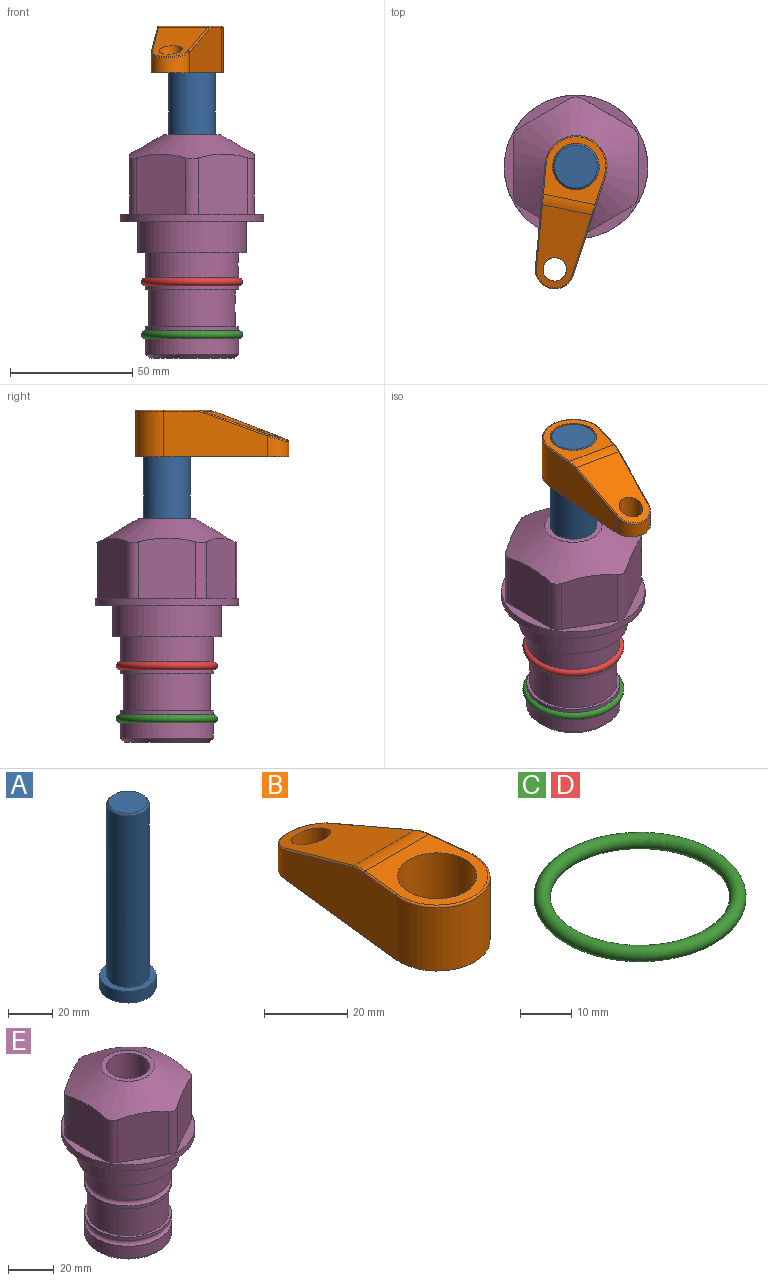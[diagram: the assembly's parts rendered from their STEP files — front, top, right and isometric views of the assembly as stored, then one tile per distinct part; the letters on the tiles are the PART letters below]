
ASSEMBLY  parts=5 mates=3
PART A: 6 faces, bbox 25.4x25.4x101.6 mm
  f0: plane 17.46x17.46mm, normal (0,0,1), area 239.5mm2, adj f5
  f1: plane 25.4x25.4mm, normal (0,0,-1), area 506.7mm2, adj f2
  f2: cylinder r=12.7mm len=25.4mm, axis (0,0,1), area 506.7mm2, adj f1,f3
  f3: plane 25.4x25.4mm, normal (0,0,1), area 221.7mm2, adj f2,f4
  f4: cylinder r=9.53mm len=94.46mm, axis (0,0,1), area 5653mm2, adj f3,f5
  f5: cone r=8.73mm half-angle=45deg, axis (0,0,-1), area 64.4mm2, adj f0,f4
PART B: 44 faces, bbox 27.5x64.5x19.1 mm
  f0: plane 2.3x0.95mm, normal (0,0,-1), area 1mm2, adj f25,f30,f34
  f1: plane 63.5x25.4mm, normal (0,0,-1), area 561.7mm2, adj f2,f3,f4,f5,f6,f7,f19,f20
  f2: cylinder r=12.7mm len=25.4mm, axis (0,0,-1), area 792.2mm2, adj f1,f3,f5,f13
  f3: plane 42.33x18.54mm, normal (0.99,0.11,0), area 647mm2, adj f1,f2,f4,f11,f12,f14
  f4: cylinder r=7.94mm len=15.78mm, axis (0,0,-1), area 158.6mm2, adj f1,f3,f5,f16
  f5: plane 42.33x18.54mm, normal (-0.99,0.11,0), area 647mm2, adj f1,f2,f4,f15,f17,f18
  f6: cylinder r=9.53mm len=19.05mm, axis (0,0,-1), area 1140.1mm2, adj f1,f8
  f7: cylinder r=4.76mm len=10.98mm, axis (0,0,-1), area 276.1mm2, adj f1,f9
  f8: plane 25.83x24.38mm, normal (0,0,1), area 262.2mm2, adj f6,f10,f11,f13,f15
  f9: plane 32.49x20.55mm, normal (0,0.34,0.94), area 489.9mm2, adj f7,f10,f14,f16,f18
  f10: cylinder r=12.7mm len=21.49mm, axis (-1,0,0), area 93.2mm2, adj f8,f9,f12,f17
  f11: cylinder r=0.51mm len=12.34mm, axis (0.11,-0.99,0), area 9.9mm2, adj f3,f8,f12,f13
  f12: bspline ~7.62x1.64mm, area 3.5mm2, adj f3,f10,f11,f14
  f13: torus R=12.19mm, axis (0,0,1), area 33.6mm2, adj f2,f8,f11,f15
  f14: cylinder r=0.51mm len=26.01mm, axis (0.1,-0.93,0.34), area 21.6mm2, adj f3,f9,f12,f16
  f15: cylinder r=0.51mm len=12.34mm, axis (0.11,0.99,0), area 9.9mm2, adj f5,f8,f13,f17
  f16: bspline ~15.78x7.05mm, area 15.7mm2, adj f4,f9,f14,f18
  f17: bspline ~7.62x1.64mm, area 3.5mm2, adj f5,f10,f15,f18
  f18: cylinder r=0.51mm len=26.01mm, axis (0.1,0.93,-0.34), area 21.6mm2, adj f5,f9,f16,f17
  f19: plane 21.6x14.29mm, normal (-0.99,-0.11,0), area 242.6mm2, adj f1,f26,f28,f34,f36,f38
  f20: plane 21.6x14.29mm, normal (0.99,-0.11,0), area 242.6mm2, adj f1,f27,f29,f37,f39,f41
  f21: cylinder r=12.7mm len=14.29mm, axis (0,0,-1), area 173.2mm2, adj f1,f26,f27,f30,f31,f33
  f22: cylinder r=7.94mm len=7.63mm, axis (0,0,-1), area 53.8mm2, adj f1,f28,f29,f42
  f23: plane 2.3x0.95mm, normal (0,0,-1), area 1mm2, adj f25,f33,f37
  f24: plane 17.94x12.32mm, normal (0,-0.34,-0.94), area 191.2mm2, adj f25,f38,f41,f42
  f25: cylinder r=9.53mm len=12.93mm, axis (-1,0,0), area 37.5mm2, adj f0,f23,f24,f31,f36,f39
  f26: cylinder r=1.59mm len=14.29mm, axis (0,0,-1), area 49mm2, adj f1,f19,f21,f32
  f27: cylinder r=1.59mm len=14.29mm, axis (0,0,-1), area 49mm2, adj f1,f20,f21,f35
  f28: cylinder r=1.59mm len=7.28mm, axis (0,0,-1), area 22.1mm2, adj f1,f19,f22,f40
  f29: cylinder r=1.59mm len=7.28mm, axis (0,0,-1), area 22.1mm2, adj f1,f20,f22,f43
  f30: torus R=14.29mm, axis (0,0,1), area 5.8mm2, adj f0,f21,f31,f32
  f31: bspline ~11.06x2.73mm, area 20.8mm2, adj f21,f25,f30,f33
  f32: sphere r=1.59mm, area 5.4mm2, adj f26,f30,f34
  f33: torus R=14.29mm, axis (0,0,1), area 5.8mm2, adj f21,f23,f31,f35
  f34: cylinder r=1.59mm len=1.68mm, axis (-0.11,0.99,0), area 2.4mm2, adj f0,f19,f32,f36
  f35: sphere r=1.59mm, area 5.4mm2, adj f27,f33,f37
  f36: bspline ~5.82x2.33mm, area 7.7mm2, adj f19,f25,f34,f38
  f37: cylinder r=1.59mm len=1.68mm, axis (0.11,0.99,0), area 2.4mm2, adj f20,f23,f35,f39
  f38: cylinder r=1.59mm len=18.33mm, axis (0.1,-0.93,0.34), area 46.7mm2, adj f19,f24,f36,f40
  f39: bspline ~5.82x2.33mm, area 7.7mm2, adj f20,f25,f37,f41
  f40: sphere r=1.59mm, area 3.6mm2, adj f28,f38,f42
  f41: cylinder r=1.59mm len=18.33mm, axis (0.1,0.93,-0.34), area 46.7mm2, adj f20,f24,f39,f43
  f42: bspline ~8.31x1.84mm, area 15.3mm2, adj f22,f24,f40,f43
  f43: sphere r=1.59mm, area 3.6mm2, adj f29,f41,f42
PART C: 1 faces, bbox 44.7x44.7x3.2 mm
  f0: torus R=19.05mm, axis (0,0,1), area 1193.9mm2
PART D: same geometry as C
PART E: 36 faces, bbox 58.7x58.7x91.2 mm
  f0: cylinder r=17.78mm len=35.56mm, axis (0,0,1), area 1670.8mm2, adj f23,f24,f31
  f1: cylinder r=19.05mm len=38.1mm, axis (0,0,1), area 1191.9mm2, adj f26,f27,f30
  f2: plane 58.66x58.66mm, normal (0,0,-1), area 1150.6mm2, adj f3,f28
  f3: cylinder r=29.33mm len=58.66mm, axis (0,0,-1), area 585.1mm2, adj f2,f4
  f4: plane 58.66x58.66mm, normal (0,0,1), area 475.9mm2, adj f3,f5,f6,f7,f8,f9,f10,f11
  f5: plane 24.5x20.32mm, normal (-0.5,0.87,0), area 562.8mm2, adj f4,f15,f16,f17
  f6: plane 24.5x20.32mm, normal (0.5,0.87,0), area 562.8mm2, adj f4,f14,f15,f17
  f7: plane 24.5x23.48mm, normal (1,0,0), area 562.8mm2, adj f4,f13,f14,f17
  f8: plane 24.5x20.32mm, normal (0.5,-0.87,0), area 562.8mm2, adj f4,f12,f13,f17
  f9: plane 24.5x20.32mm, normal (-0.5,-0.87,0), area 562.8mm2, adj f4,f11,f12,f17
  f10: plane 24.5x23.48mm, normal (-1,0,0), area 562.8mm2, adj f4,f11,f16,f17
  f11: cylinder r=5.08mm len=23.01mm, axis (0,0,-1), area 121.2mm2, adj f4,f9,f10,f17
  f12: cylinder r=5.08mm len=23.01mm, axis (0,0,-1), area 121.2mm2, adj f4,f8,f9,f17
  f13: cylinder r=5.08mm len=23.01mm, axis (0,0,-1), area 121.2mm2, adj f4,f7,f8,f17
  f14: cylinder r=5.08mm len=23.01mm, axis (0,0,-1), area 121.2mm2, adj f4,f6,f7,f17
  f15: cylinder r=5.08mm len=23.01mm, axis (0,0,-1), area 121.2mm2, adj f4,f5,f6,f17
  f16: cylinder r=5.08mm len=23.01mm, axis (0,0,-1), area 121.2mm2, adj f4,f5,f10,f17
  f17: cone r=11.73mm half-angle=60deg, axis (0,0,-1), area 2071.8mm2, adj f5,f6,f7,f8,f9,f10,f11,f12
  f18: plane 23.46x23.46mm, normal (0,0,1), area 147.4mm2, adj f17,f35
  f19: plane 34.93x34.93mm, normal (0,0,-1), area 958mm2, adj f29
  f20: cylinder r=19.05mm len=38.1mm, axis (0,0,1), area 760.1mm2, adj f21,f29
  f21: torus R=19.05mm, axis (0,0,1), area 565.3mm2, adj f20,f22
  f22: cylinder r=19.05mm len=38.1mm, axis (0,0,1), area 190mm2, adj f21,f23
  f23: plane 38.1x38.1mm, normal (0,0,1), area 146.9mm2, adj f0,f22
  f24: plane 38.1x38.1mm, normal (0,0,-1), area 146.9mm2, adj f0,f25
  f25: cylinder r=19.05mm len=38.1mm, axis (0,0,1), area 190mm2, adj f24,f26
  f26: torus R=19.05mm, axis (0,0,1), area 565.3mm2, adj f1,f25
  f27: plane 44.45x44.45mm, normal (0,0,-1), area 411.7mm2, adj f1,f28
  f28: cylinder r=22.23mm len=44.45mm, axis (0,0,1), area 1773.5mm2, adj f2,f27
  f29: cone r=19.05mm half-angle=45deg, axis (0,0,1), area 257.5mm2, adj f19,f20
  f30: cylinder r=3.17mm len=6.75mm, axis (-1,0,0), area 128mm2, adj f1,f33
  f31: cylinder r=3.17mm len=6.35mm, axis (-1,0,0), area 102.5mm2, adj f0,f33
  f32: plane 25.4x25.4mm, normal (0,0,1), area 506.7mm2, adj f33
  f33: cylinder r=12.7mm len=66.42mm, axis (0,0,-1), area 5236.2mm2, adj f30,f31,f32,f34
  f34: cone r=9.53mm half-angle=30deg, axis (0,0,-1), area 443.4mm2, adj f33,f35
  f35: cylinder r=9.53mm len=19.05mm, axis (0,0,-1), area 849mm2, adj f18,f34
PLACE A rot(axis=(0,0,-1),101.7deg) t=(0,0,6.38)mm
PLACE B rot(axis=(0,0,1),168.3deg) t=(0,0,60.99)mm
PLACE C t=(0,0,-21.59)mm
PLACE D at identity
PLACE E at identity fixed
MATE fastened C.f0 <-> E.f0  axis (0,0,1) through (0,0,-46.1)mm
MATE cylindrical A.f2 <-> E.f0  axis (0,0,1) through (0,0,32.01)mm
MATE fastened B.f2 <-> A.f2  axis (0,0,1) through (0,0,80.04)mm
